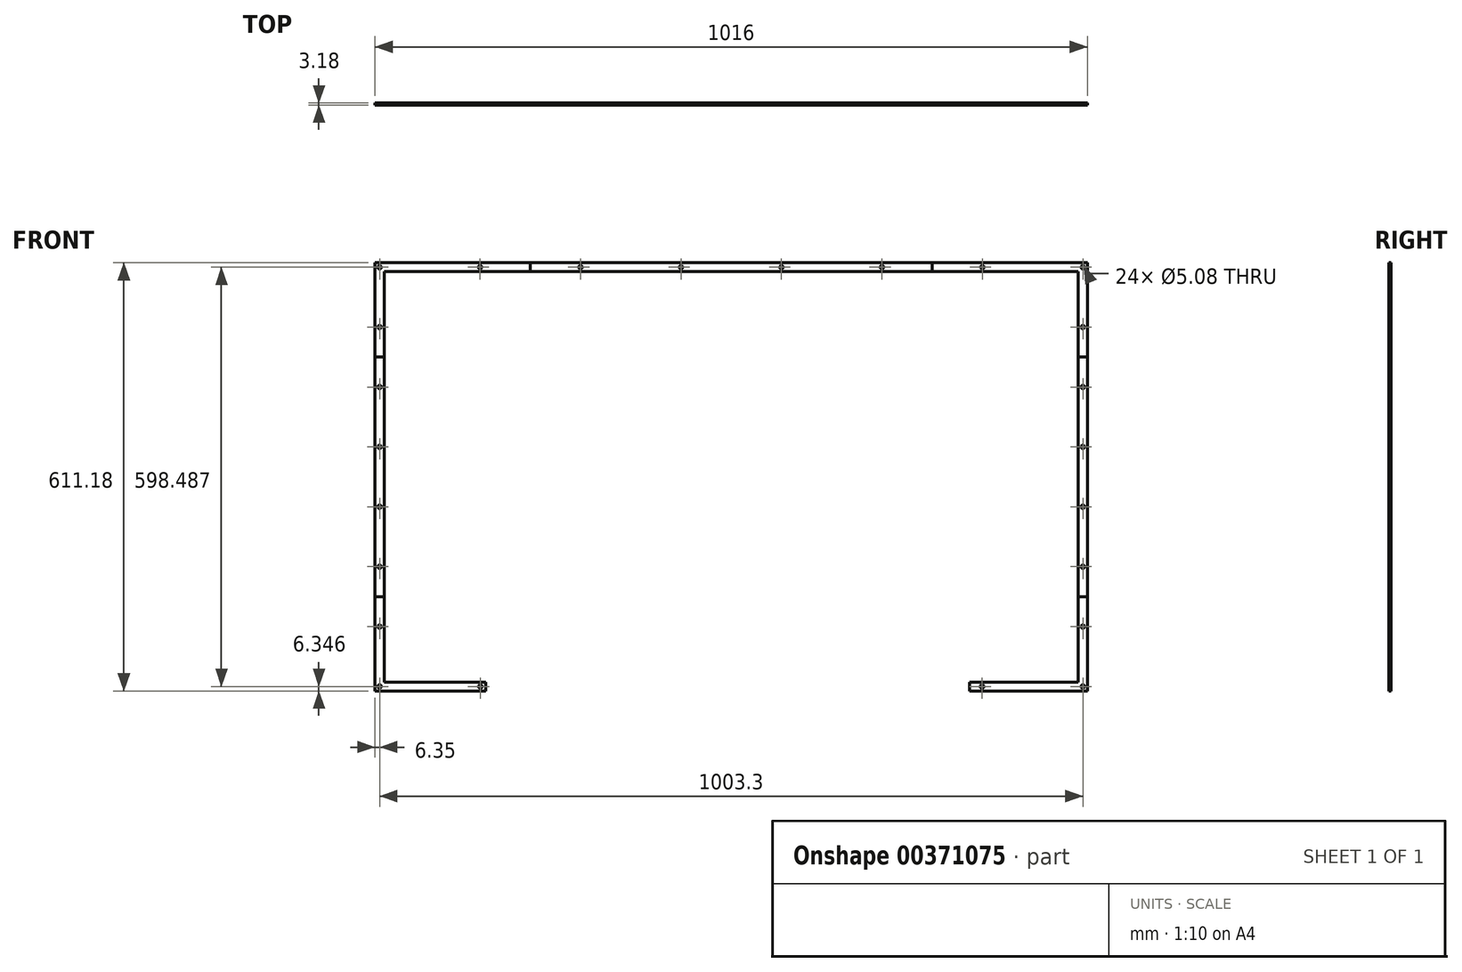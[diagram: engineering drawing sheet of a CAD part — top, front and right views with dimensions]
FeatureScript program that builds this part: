
annotation { "Feature Type Name" : "Feature", "Feature Type Description" : "" }
export const myFeature = defineFeature(function(context is Context, id is Id, definition is map)
    precondition{}
    {
        {
            var Q0;
            Q0=qCreatedBy(makeId("Front.planeOp"),FACE);
            var sketch = newSketch(context, id + "F0", { "sketchPlane" : qUnion([Q0])});
            skLineSegment(sketch, "E0.bottom", {"start": v(495.3, 292.9) * mm, "end": v(-495.3, 292.9) * mm});
            skLineSegment(sketch, "E0.top", {"start": v(495.3, -292.9) * mm, "end": v(-495.3, -292.9) * mm});
            skLineSegment(sketch, "E0.left", {"start": v(495.3, 292.9) * mm, "end": v(495.3, -292.9) * mm});
            skLineSegment(sketch, "E0.right", {"start": v(-495.3, 292.9) * mm, "end": v(-495.3, -292.9) * mm});
            skPoint(sketch, "E0.middle", {"position": v(0, 0) * mm});
            skLineSegment(sketch, "E1.0", {"start": v(-508, 305.6) * mm, "end": v(-508, -305.6) * mm});
            skLineSegment(sketch, "E1.1", {"start": v(508, 305.6) * mm, "end": v(-508, 305.6) * mm});
            skLineSegment(sketch, "E1.2", {"start": v(508, 305.6) * mm, "end": v(508, -305.6) * mm});
            skLineSegment(sketch, "E1.3", {"start": v(508, -305.6) * mm, "end": v(-508, -305.6) * mm});
            skLineSegment(sketch, "E2", {"start": v(-508, 305.6) * mm, "end": v(-495.3, 292.9) * mm});
            skPoint(sketch, "E3.middle", {"position": v(-501.65, 299.24) * mm});
            skLineSegment(sketch, "E4", {"start": v(-350.3, -292.9) * mm, "end": v(-350.3, -305.6) * mm});
            skLineSegment(sketch, "E5", {"start": v(340.3, -292.9) * mm, "end": v(340.3, -305.6) * mm});
            skLineSegment(sketch, "E6", {"start": v(-495.3, -292.9) * mm, "end": v(-508, -305.6) * mm});
            skLineSegment(sketch, "E7", {"start": v(495.3, -292.9) * mm, "end": v(508, -305.6) * mm});
            skLineSegment(sketch, "E8", {"start": v(495.3, 292.9) * mm, "end": v(508, 305.6) * mm});
            skPoint(sketch, "E9.middle", {"position": v(-357.84, -299.24) * mm});
            skPoint(sketch, "E10", {"position": v(-501.65, -299.24) * mm});
            skPoint(sketch, "E11", {"position": v(501.65, -299.24) * mm});
            skPoint(sketch, "E12", {"position": v(501.65, 299.24) * mm});
            skPoint(sketch, "E13", {"position": v(-501.65, 213.75) * mm});
            skPoint(sketch, "E14", {"position": v(-501.65, 128.25) * mm});
            skPoint(sketch, "E15", {"position": v(-501.65, 42.75) * mm});
            skPoint(sketch, "E16", {"position": v(-501.65, -42.75) * mm});
            skPoint(sketch, "E17", {"position": v(-501.65, -128.25) * mm});
            skPoint(sketch, "E18", {"position": v(-501.65, -213.75) * mm});
            skPoint(sketch, "E19.MirrorP", {"position": v(501.65, 213.75) * mm});
            skPoint(sketch, "E20.MirrorP", {"position": v(501.65, 128.25) * mm});
            skPoint(sketch, "E21.MirrorP", {"position": v(501.65, 42.75) * mm});
            skPoint(sketch, "E22.MirrorP", {"position": v(501.65, -42.75) * mm});
            skPoint(sketch, "E23.MirrorP", {"position": v(501.65, -128.25) * mm});
            skPoint(sketch, "E24.MirrorP", {"position": v(501.65, -213.75) * mm});
            skPoint(sketch, "E25", {"position": v(-358.32, 299.24) * mm});
            skPoint(sketch, "E26.middle", {"position": v(-215, 299.24) * mm});
            skPoint(sketch, "E27.middle", {"position": v(-71.66, 299.24) * mm});
            skPoint(sketch, "E28.middle", {"position": v(71.66, 299.24) * mm});
            skPoint(sketch, "E29.middle", {"position": v(215, 299.24) * mm});
            skPoint(sketch, "E30.middle", {"position": v(358.32, 299.24) * mm});
            skPoint(sketch, "E31", {"position": v(357.84, -299.24) * mm});
            skCircle(sketch, "E32", {"center": v(-501.65, 299.24) * mm, "radius": 2.54 * mm});
            skCircle(sketch, "E33", {"center": v(-358.32, 299.24) * mm, "radius": 2.54 * mm});
            skCircle(sketch, "E34", {"center": v(-215, 299.24) * mm, "radius": 2.54 * mm});
            skCircle(sketch, "E35", {"center": v(-71.66, 299.24) * mm, "radius": 2.54 * mm});
            skCircle(sketch, "E36", {"center": v(71.66, 299.24) * mm, "radius": 2.54 * mm});
            skCircle(sketch, "E37", {"center": v(215, 299.24) * mm, "radius": 2.54 * mm});
            skCircle(sketch, "E38", {"center": v(-501.65, 213.75) * mm, "radius": 2.54 * mm});
            skCircle(sketch, "E39", {"center": v(-501.65, 128.25) * mm, "radius": 2.54 * mm});
            skCircle(sketch, "E40", {"center": v(-501.65, 42.75) * mm, "radius": 2.54 * mm});
            skCircle(sketch, "E41", {"center": v(-501.65, -42.75) * mm, "radius": 2.54 * mm});
            skCircle(sketch, "E42", {"center": v(358.32, 299.24) * mm, "radius": 2.54 * mm});
            skCircle(sketch, "E43", {"center": v(501.65, 299.24) * mm, "radius": 2.54 * mm});
            skCircle(sketch, "E44", {"center": v(501.65, 213.75) * mm, "radius": 2.54 * mm});
            skCircle(sketch, "E45", {"center": v(501.65, 128.25) * mm, "radius": 2.54 * mm});
            skCircle(sketch, "E46", {"center": v(501.65, 42.75) * mm, "radius": 2.54 * mm});
            skCircle(sketch, "E47", {"center": v(501.65, -42.75) * mm, "radius": 2.54 * mm});
            skCircle(sketch, "E48", {"center": v(501.65, -128.25) * mm, "radius": 2.54 * mm});
            skCircle(sketch, "E49", {"center": v(501.65, -213.75) * mm, "radius": 2.54 * mm});
            skCircle(sketch, "E50", {"center": v(501.65, -299.24) * mm, "radius": 2.54 * mm});
            skCircle(sketch, "E51", {"center": v(357.84, -299.24) * mm, "radius": 2.54 * mm});
            skCircle(sketch, "E52", {"center": v(-357.84, -299.24) * mm, "radius": 2.54 * mm});
            skCircle(sketch, "E53", {"center": v(-501.65, -299.24) * mm, "radius": 2.54 * mm});
            skCircle(sketch, "E54", {"center": v(-501.65, -213.75) * mm, "radius": 2.54 * mm});
            skCircle(sketch, "E55", {"center": v(-501.65, -128.25) * mm, "radius": 2.54 * mm});
            skLineSegment(sketch, "E56", {"start": v(-358.32, 299.24) * mm, "end": v(-215, 299.24) * mm});
            skLineSegment(sketch, "E57", {"start": v(-286.66, 305.6) * mm, "end": v(-286.66, 292.9) * mm});
            skPoint(sketch, "E57.startSnap0", {"position": v(-286.66, 299.24) * mm});
            skLineSegment(sketch, "E58.MirrorCS", {"start": v(286.66, 305.6) * mm, "end": v(286.66, 292.9) * mm});
            skLineSegment(sketch, "E59", {"start": v(-501.65, 213.75) * mm, "end": v(-501.65, 128.25) * mm});
            skLineSegment(sketch, "E60", {"start": v(-508, 171) * mm, "end": v(-495.3, 171) * mm});
            skPoint(sketch, "E60.startSnap0", {"position": v(-501.65, 171) * mm});
            skLineSegment(sketch, "E61.MirrorCS", {"start": v(-508, -171) * mm, "end": v(-495.3, -171) * mm});
            skLineSegment(sketch, "E62.MirrorCS", {"start": v(508, 171) * mm, "end": v(495.3, 171) * mm});
            skLineSegment(sketch, "E63.MirrorCS", {"start": v(508, -171) * mm, "end": v(495.3, -171) * mm});
            skSolve(sketch);
        }
        {
            var Q0;
            Q0=makeQuery(id+"F0.imprint","IMPRINT",FACE,{"disambiguationData":[TD([[makeQuery(id+"F0.imprint","IMPRINT",EDGE,{"derivedFrom":sQuery(id+"F0.wireOp",EDGE,"E38")}),-1.0]])]});
            var Q1;
            Q1=makeQuery(id+"F0.imprint","IMPRINT",FACE,{"disambiguationData":[TD([[makeQuery(id+"F0.imprint","IMPRINT",EDGE,{"derivedFrom":sQuery(id+"F0.wireOp",EDGE,"E33")}),-1.0]])]});
            extrude(context, id + "F1", {"entities" : qUnion([Q0, Q1]), "endBound" : BoundingType.SYMMETRIC, "depth" : 3.17 * mm});
        }
        {
            var Q0;
            Q0=makeQuery(id+"F0.imprint","IMPRINT",FACE,{"disambiguationData":[TD([[makeQuery(id+"F0.imprint","IMPRINT",EDGE,{"derivedFrom":sQuery(id+"F0.wireOp",EDGE,"E34")}),-1.0]])]});
            extrude(context, id + "F2", {"entities" : qUnion([Q0]), "endBound" : BoundingType.SYMMETRIC, "depth" : 3.17 * mm});
        }
        {
            var Q0;
            Q0=makeQuery(id+"F0.imprint","IMPRINT",FACE,{"disambiguationData":[TD([[makeQuery(id+"F0.imprint","IMPRINT",EDGE,{"derivedFrom":sQuery(id+"F0.wireOp",EDGE,"E42")}),-1.0]])]});
            var Q1;
            Q1=makeQuery(id+"F0.imprint","IMPRINT",FACE,{"disambiguationData":[TD([[makeQuery(id+"F0.imprint","IMPRINT",EDGE,{"derivedFrom":sQuery(id+"F0.wireOp",EDGE,"E44")}),-1.0]])]});
            extrude(context, id + "F3", {"entities" : qUnion([Q0, Q1]), "endBound" : BoundingType.SYMMETRIC, "depth" : 3.17 * mm});
        }
        {
            var Q0;
            Q0=makeQuery(id+"F0.imprint","IMPRINT",FACE,{"disambiguationData":[TD([[makeQuery(id+"F0.imprint","IMPRINT",EDGE,{"derivedFrom":sQuery(id+"F0.wireOp",EDGE,"E45")}),-1.0]])]});
            extrude(context, id + "F4", {"entities" : qUnion([Q0]), "endBound" : BoundingType.SYMMETRIC, "depth" : 3.17 * mm});
        }
        {
            var Q0;
            Q0=makeQuery(id+"F0.imprint","IMPRINT",FACE,{"disambiguationData":[TD([[makeQuery(id+"F0.imprint","IMPRINT",EDGE,{"derivedFrom":sQuery(id+"F0.wireOp",EDGE,"E49")}),-1.0]])]});
            var Q1;
            {var subQ7=sQuery(id+"F0.wireOp",EDGE,"E5");Q1=makeQuery(id+"F0.imprint","IMPRINT",FACE,{"disambiguationData":[TD([[makeQuery(id+"F0.imprint","IMPRINT",EDGE,{"derivedFrom":subQ7}),1.0]])]});}
            extrude(context, id + "F5", {"entities" : qUnion([Q0, Q1]), "endBound" : BoundingType.SYMMETRIC, "depth" : 3.17 * mm});
        }
        {
            var Q0;
            {var subQ5=sQuery(id+"F0.wireOp",EDGE,"E4");Q0=makeQuery(id+"F0.imprint","IMPRINT",FACE,{"disambiguationData":[TD([[makeQuery(id+"F0.imprint","IMPRINT",EDGE,{"derivedFrom":subQ5}),-1.0]])]});}
            var Q1;
            Q1=makeQuery(id+"F0.imprint","IMPRINT",FACE,{"disambiguationData":[TD([[makeQuery(id+"F0.imprint","IMPRINT",EDGE,{"derivedFrom":sQuery(id+"F0.wireOp",EDGE,"E54")}),-1.0]])]});
            extrude(context, id + "F6", {"entities" : qUnion([Q0, Q1]), "endBound" : BoundingType.SYMMETRIC, "depth" : 3.17 * mm});
        }
        {
            var Q0;
            Q0=makeQuery(id+"F0.imprint","IMPRINT",FACE,{"disambiguationData":[TD([[makeQuery(id+"F0.imprint","IMPRINT",EDGE,{"derivedFrom":sQuery(id+"F0.wireOp",EDGE,"E39")}),-1.0]])]});
            extrude(context, id + "F7", {"entities" : qUnion([Q0]), "endBound" : BoundingType.SYMMETRIC, "depth" : 3.17 * mm});
        }
    });
